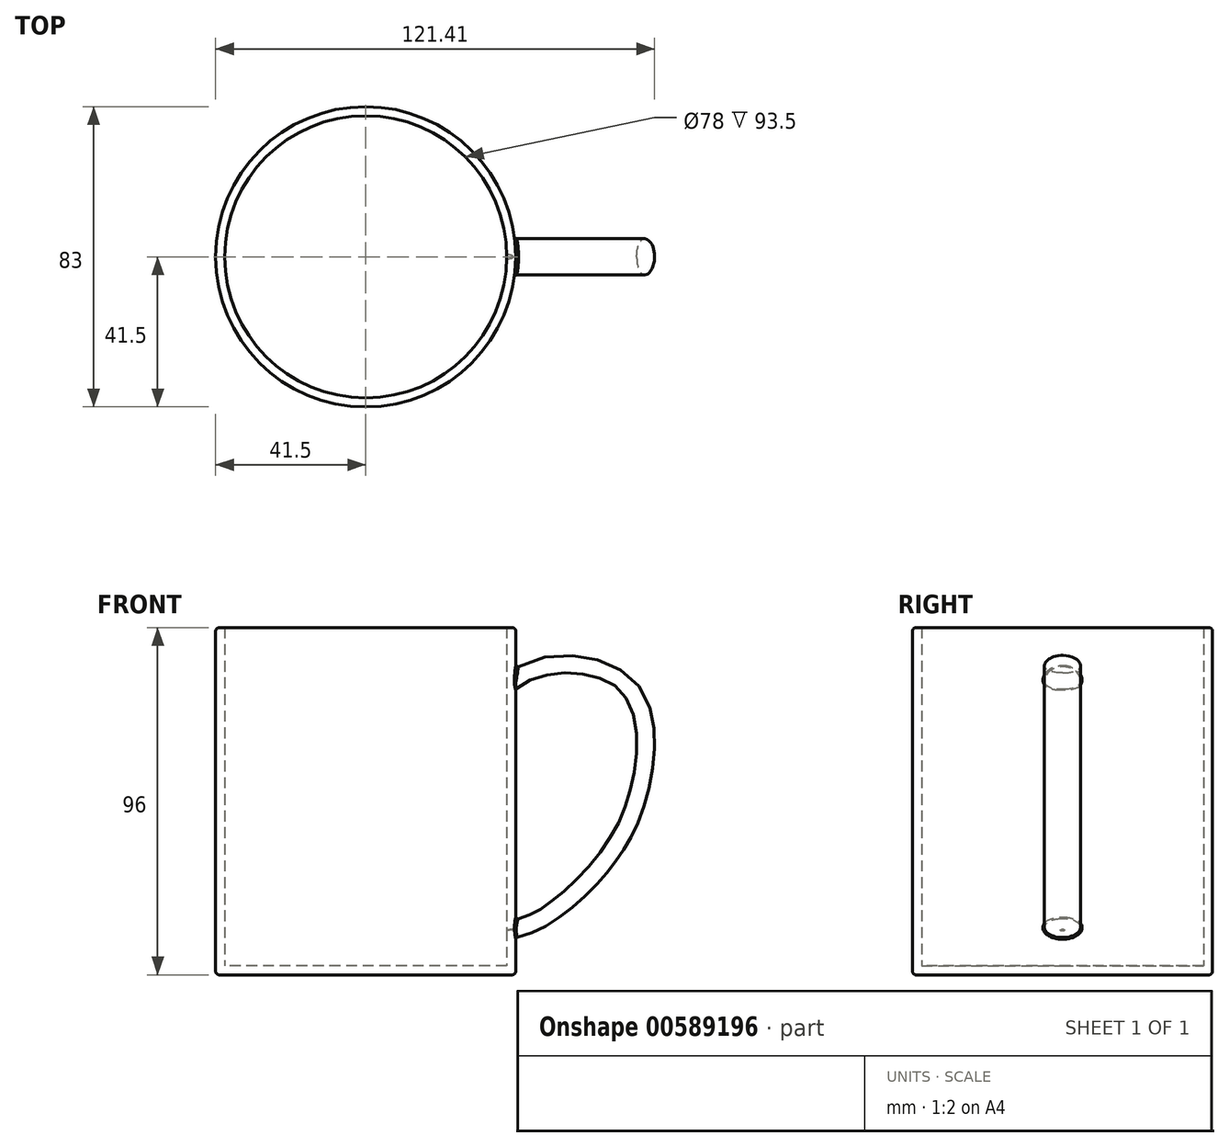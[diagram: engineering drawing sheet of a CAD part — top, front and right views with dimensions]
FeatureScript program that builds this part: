
annotation { "Feature Type Name" : "Feature", "Feature Type Description" : "" }
export const myFeature = defineFeature(function(context is Context, id is Id, definition is map)
    precondition{}
    {
        {
            var Q0;
            Q0=qCreatedBy(makeId("Top.planeOp"),FACE);
            var sketch = newSketch(context, id + "F0", { "sketchPlane" : qUnion([Q0])});
            skCircle(sketch, "E0", {"center": v(0, 0) * mm, "radius": 41.5 * mm});
            skSolve(sketch);
        }
        {
            var Q0;
            Q0=makeQuery(id+"F0.imprint","IMPRINT",FACE,{"disambiguationData":[TD([[makeQuery(id+"F0.imprint","IMPRINT",EDGE,{"derivedFrom":sQuery(id+"F0.wireOp",EDGE,"E0")}),1.0]])]});
            extrude(context, id + "F1", {"entities" : qUnion([Q0]), "depth" : 96 * mm, "offsetDistance" : 25 * mm});
        }
        {
            var Q0;
            Q0=qCreatedBy(makeId("Front.planeOp"),FACE);
            var sketch = newSketch(context, id + "F2", { "sketchPlane" : qUnion([Q0])});
            skFitSpline(sketch, "E1", {"points": [v(33.75, 71.24) * mm, v(49.17, 84.1) * mm, v(72.14, 78.26) * mm, v(75.1, 52.34) * mm, v(64.49, 30.78) * mm, v(47.24, 15.96) * mm, v(35.25, 12.75) * mm], "startDerivative": vector(65.92, 115.32) * mm, "endDerivative": vector(-91.77, -9.2) * mm});
            skSolve(sketch);
        }
        {
            var Q0;
            Q0=qCreatedBy(makeId("Right.planeOp"),FACE);
            cPlane(context, id + "F3", {"entities" : qUnion([Q0]), "cplaneType" : CPlaneType.OFFSET, "offset" : 33 * mm, "width" : 150 * mm, "height" : 150 * mm});
        }
        {
            var Q0;
            Q0=qCreatedBy(id+"F3.planeOp",FACE);
            var sketch = newSketch(context, id + "F4", { "sketchPlane" : qUnion([Q0])});
            skCircle(sketch, "E2", {"center": v(0, 71.39) * mm, "radius": 5 * mm});
            skSolve(sketch);
        }
        {
            var Q0;
            Q0 = qSketchRegion(id + "F4", true);
            var Q1;
            Q1=sQuery(id+"F2.wireOp",EDGE,"E1");
            sweep(context, id + "F5", {"operationType" : NewBodyOperationType.ADD, "profiles" : qUnion([Q0]), "path" : qUnion([Q1])});
        }
        {
            var Q0;
            Q0=makeQuery(id+"F1.opExtrude","CAP_FACE",FACE,{"disambiguationData":[OSD([sQuery(id+"F0.wireOp",EDGE,"E0")])],"isStart":false});
            shell(context, id + "F6", {"entities" : qUnion([Q0]), "thickness" : 2.5 * mm});
        }
        {
            var Q0;
            Q0=makeQuery(id+"F1.opExtrude","CAP_EDGE",EDGE,{"disambiguationData":[OSD([sQuery(id+"F0.wireOp",EDGE,"E0")])],"isStart":false});
            var Q1;
            Q1=makeQuery(id+"F1.opExtrude","CAP_EDGE",EDGE,{"disambiguationData":[OSD([sQuery(id+"F0.wireOp",EDGE,"E0")])],"isStart":true});
            fillet(context, id + "F7", {"entities" : qUnion([Q0, Q1]), "radius" : 1 * mm, "tangentPropagation" : true, "allowEdgeOverflow" : false});
        }
        {
            var Q0;
            Q0=makeQuery(id+"F5.boolean.opBoolean","INTERSECT",EDGE,{"disambiguationData":[OD(1.0)],"derivedFrom":[makeQuery(id+"F1.opExtrude","SWEPT_FACE",FACE,{"disambiguationData":[OSD([sQuery(id+"F0.wireOp",EDGE,"E0")])]}),makeQuery(id+"F5.opSweep","SWEPT_FACE",FACE,{"disambiguationData":[OSD([sQuery(id+"F2.wireOp",EDGE,"E1"),sQuery(id+"F4.wireOp",EDGE,"E2")])]})]});
            var Q1;
            Q1=makeQuery(id+"F5.boolean.opBoolean","INTERSECT",EDGE,{"disambiguationData":[OD(0.0)],"derivedFrom":[makeQuery(id+"F1.opExtrude","SWEPT_FACE",FACE,{"disambiguationData":[OSD([sQuery(id+"F0.wireOp",EDGE,"E0")])]}),makeQuery(id+"F5.opSweep","SWEPT_FACE",FACE,{"disambiguationData":[OSD([sQuery(id+"F2.wireOp",EDGE,"E1"),sQuery(id+"F4.wireOp",EDGE,"E2")])]})]});
            chamfer(context, id + "F8", {"entities" : qUnion([Q0, Q1]), "width" : .5 * mm, "tangentPropagation" : true});
        }
    });
